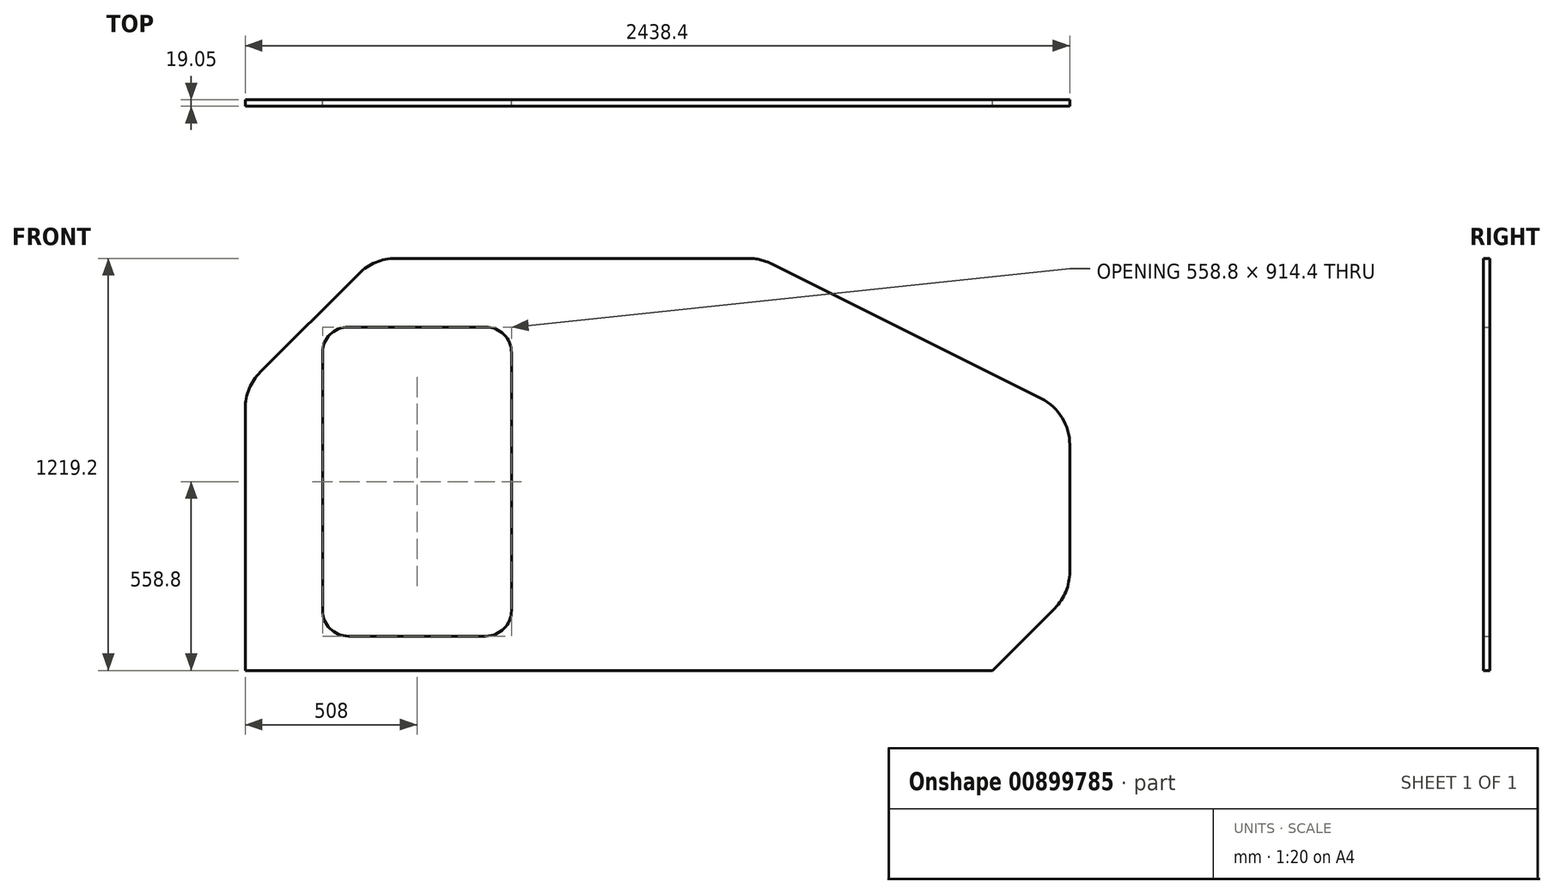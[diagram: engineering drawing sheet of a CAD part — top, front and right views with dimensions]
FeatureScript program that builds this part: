
annotation { "Feature Type Name" : "Feature", "Feature Type Description" : "" }
export const myFeature = defineFeature(function(context is Context, id is Id, definition is map)
    precondition{}
    {
        {
            var Q0;
            Q0=qCreatedBy(makeId("Front.planeOp"),FACE);
            var sketch = newSketch(context, id + "F0", { "sketchPlane" : qUnion([Q0])});
            skLineSegment(sketch, "E0.bottom", {"start": v(268.82, 609.6) * mm, "end": v(-775.07, 609.6) * mm});
            skLineSegment(sketch, "E0.top", {"start": v(990.6, -609.6) * mm, "end": v(-1219.2, -609.6) * mm});
            skLineSegment(sketch, "E0.left", {"start": v(1219.2, 58.21) * mm, "end": v(1219.2, -317.87) * mm});
            skLineSegment(sketch, "E0.right", {"start": v(-1219.2, 165.47) * mm, "end": v(-1219.2, -609.6) * mm});
            skPoint(sketch, "E0.middle", {"position": v(0, 0) * mm});
            skLineSegment(sketch, "E1", {"start": v(-1174.56, 273.24) * mm, "end": v(-882.84, 564.96) * mm});
            skLineSegment(sketch, "E2", {"start": v(336.98, 593.51) * mm, "end": v(1134.96, 194.52) * mm});
            skLineSegment(sketch, "E3", {"start": v(1174.56, -425.64) * mm, "end": v(990.6, -609.6) * mm});
            skLineSegment(sketch, "E4.bottom", {"start": v(-914.4, 406.4) * mm, "end": v(-508, 406.4) * mm});
            skLineSegment(sketch, "E4.top", {"start": v(-914.4, -508) * mm, "end": v(-508, -508) * mm});
            skLineSegment(sketch, "E4.left", {"start": v(-990.6, 330.2) * mm, "end": v(-990.6, -431.8) * mm});
            skLineSegment(sketch, "E4.right", {"start": v(-431.8, 330.2) * mm, "end": v(-431.8, -431.8) * mm});
            skPoint(sketch, "E5.visualSharp", {"position": v(-990.6, 406.4) * mm});
            skArc(sketch, "E5.filletArc", {"start": v(-914.4, 406.4) * mm, "mid": v(-968.28, 384.08) * mm, "end": v(-990.6, 330.2) * mm});
            skPoint(sketch, "E6.visualSharp", {"position": v(-431.8, 406.4) * mm});
            skArc(sketch, "E6.filletArc", {"start": v(-431.8, 330.2) * mm, "mid": v(-454.12, 384.08) * mm, "end": v(-508, 406.4) * mm});
            skPoint(sketch, "E7.visualSharp", {"position": v(-431.8, -508) * mm});
            skArc(sketch, "E7.filletArc", {"start": v(-508, -508) * mm, "mid": v(-454.12, -485.68) * mm, "end": v(-431.8, -431.8) * mm});
            skPoint(sketch, "E8.visualSharp", {"position": v(-990.6, -508) * mm});
            skArc(sketch, "E8.filletArc", {"start": v(-990.6, -431.8) * mm, "mid": v(-968.28, -485.68) * mm, "end": v(-914.4, -508) * mm});
            skPoint(sketch, "E9.orphan", {"position": v(-1219.2, 609.6) * mm});
            skPoint(sketch, "E10.orphan", {"position": v(1219.2, 609.6) * mm});
            skPoint(sketch, "E11.orphan", {"position": v(1219.2, -609.6) * mm});
            skPoint(sketch, "E12.visualSharp", {"position": v(-838.2, 609.6) * mm});
            skArc(sketch, "E12.filletArc", {"start": v(-775.07, 609.6) * mm, "mid": v(-833.4, 598) * mm, "end": v(-882.84, 564.96) * mm});
            skPoint(sketch, "E13.visualSharp", {"position": v(-1219.2, 228.6) * mm});
            skArc(sketch, "E13.filletArc", {"start": v(-1174.56, 273.24) * mm, "mid": v(-1207.6, 223.8) * mm, "end": v(-1219.2, 165.47) * mm});
            skPoint(sketch, "E14.visualSharp", {"position": v(304.8, 609.6) * mm});
            skArc(sketch, "E14.filletArc", {"start": v(336.98, 593.51) * mm, "mid": v(303.84, 605.52) * mm, "end": v(268.82, 609.6) * mm});
            skPoint(sketch, "E15.visualSharp", {"position": v(1219.2, 152.4) * mm});
            skArc(sketch, "E15.filletArc", {"start": v(1219.2, 58.21) * mm, "mid": v(1196.44, 138.33) * mm, "end": v(1134.96, 194.52) * mm});
            skPoint(sketch, "E16.visualSharp", {"position": v(1219.2, -381) * mm});
            skArc(sketch, "E16.filletArc", {"start": v(1174.56, -425.64) * mm, "mid": v(1207.6, -376.2) * mm, "end": v(1219.2, -317.87) * mm});
            skSolve(sketch);
        }
        {
            var Q0;
            Q0=makeQuery(id+"F0.imprint","IMPRINT",FACE,{"disambiguationData":[TD([[makeQuery(id+"F0.imprint","IMPRINT",EDGE,{"derivedFrom":sQuery(id+"F0.wireOp",EDGE,"E0.bottom")}),1.0]])]});
            extrude(context, id + "F1", {"entities" : qUnion([Q0]), "depth" : 19.05 * mm, "offsetDistance" : 25.4 * mm});
        }
    });
